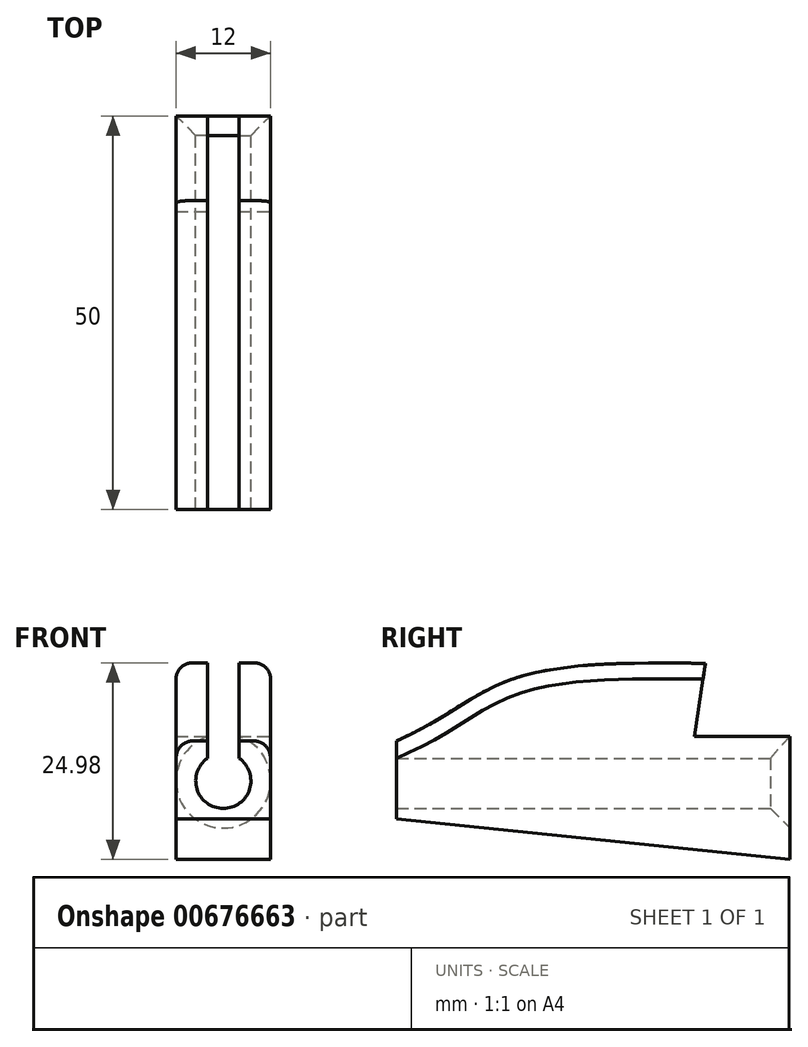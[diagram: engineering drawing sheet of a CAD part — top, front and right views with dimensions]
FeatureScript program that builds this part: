
annotation { "Feature Type Name" : "Feature", "Feature Type Description" : "" }
export const myFeature = defineFeature(function(context is Context, id is Id, definition is map)
    precondition{}
    {
        {
            var Q0;
            Q0=qCreatedBy(makeId("Top.planeOp"),FACE);
            var sketch = newSketch(context, id + "F0", { "sketchPlane" : qUnion([Q0])});
            skLineSegment(sketch, "E0.bottom", {"start": v(-6, 0) * mm, "end": v(6, 0) * mm});
            skLineSegment(sketch, "E0.top", {"start": v(-6, -50) * mm, "end": v(6, -50) * mm});
            skLineSegment(sketch, "E0.left", {"start": v(-6, 0) * mm, "end": v(-6, -50) * mm});
            skLineSegment(sketch, "E0.right", {"start": v(6, 0) * mm, "end": v(6, -50) * mm});
            skSolve(sketch);
        }
        {
            var Q0;
            Q0=makeQuery(id+"F0.imprint","IMPRINT",FACE,{"disambiguationData":[TD([[makeQuery(id+"F0.imprint","IMPRINT",EDGE,{"derivedFrom":sQuery(id+"F0.wireOp",EDGE,"E0.bottom")}),-1.0]])]});
            extrude(context, id + "F1", {"entities" : qUnion([Q0]), "depth" : 30 * mm, "offsetDistance" : 25 * mm});
        }
        {
            var Q0;
            Q0=qCreatedBy(makeId("Front.planeOp"),FACE);
            var sketch = newSketch(context, id + "F2", { "sketchPlane" : qUnion([Q0])});
            skCircle(sketch, "E1", {"center": v(0, 10) * mm, "radius": 3.5 * mm});
            skSolve(sketch);
        }
        {
            var Q0;
            Q0=sQuery(id+"F2.wireOp",VERTEX,"E1.center");
            var Q1;
            Q1=makeQuery(id+"F1.opExtrude","SWEPT_BODY",BODY,{"disambiguationData":[OSD([sQuery(id+"F0.wireOp",EDGE,"E0.bottom"),sQuery(id+"F0.wireOp",EDGE,"E0.top"),sQuery(id+"F0.wireOp",EDGE,"E0.left"),sQuery(id+"F0.wireOp",EDGE,"E0.right")])]});
            hole(context, id + "F3", {"style" : HoleStyle.C_SINK, "endStyle" : HoleEndStyle.THROUGH, "oppositeDirection" : true, "holeDiameter" : 7 * mm, "cSinkDiameter" : 12 * mm, "cSinkAngle" : 90 * degree, "majorDiameter" : 5 * mm, "isTappedThrough" : true, "tappedDepth" : 12 * mm, "tapClearance" : 3, "locations" : qUnion([Q0]), "scope" : qUnion([Q1])});
        }
        {
            var Q0;
            Q0=qCreatedBy(makeId("Front.planeOp"),FACE);
            var sketch = newSketch(context, id + "F4", { "sketchPlane" : qUnion([Q0])});
            skLineSegment(sketch, "E2.bottom", {"start": v(2, 30) * mm, "end": v(-2, 30) * mm});
            skLineSegment(sketch, "E2.top", {"start": v(2, 12.87) * mm, "end": v(-2, 12.87) * mm});
            skLineSegment(sketch, "E2.left", {"start": v(2, 30) * mm, "end": v(2, 12.87) * mm});
            skLineSegment(sketch, "E2.right", {"start": v(-2, 30) * mm, "end": v(-2, 12.87) * mm});
            skSolve(sketch);
        }
        {
            var Q0;
            Q0=makeQuery(id+"F4.imprint","IMPRINT",FACE,{"disambiguationData":[TD([[makeQuery(id+"F4.imprint","IMPRINT",EDGE,{"derivedFrom":sQuery(id+"F4.wireOp",EDGE,"E2.bottom")}),1.0]])]});
            extrude(context, id + "F5", {"entities" : qUnion([Q0]), "operationType" : NewBodyOperationType.REMOVE, "depth" : 50 * mm, "offsetDistance" : 25 * mm});
        }
        {
            var Q0;
            Q0=qCreatedBy(makeId("Right.planeOp"),FACE);
            var sketch = newSketch(context, id + "F6", { "sketchPlane" : qUnion([Q0])});
            skLineSegment(sketch, "E3", {"start": v(0, 15.66) * mm, "end": v(-12.16, 15.66) * mm});
            skLineSegment(sketch, "E4", {"start": v(-12.16, 15.66) * mm, "end": v(-10.75, 24.93) * mm});
            skSolve(sketch);
        }
        {
            var Q0;
            Q0=qCreatedBy(makeId("Right.planeOp"),FACE);
            var sketch = newSketch(context, id + "F7", { "sketchPlane" : qUnion([Q0])});
            skFitSpline(sketch, "E5", {"points": [v(-10.75, 24.93) * mm, v(-34.14, 22.02) * mm, v(-50, 15.06) * mm], "startDerivative": vector(-44.86, 0.18) * mm, "endDerivative": vector(-35.7, -18.77) * mm});
            skSolve(sketch);
        }
        {
            var Q0;
            Q0=qCreatedBy(makeId("Right.planeOp"),FACE);
            var sketch = newSketch(context, id + "F8", { "sketchPlane" : qUnion([Q0])});
            skLineSegment(sketch, "E6.0", {"start": v(0, 15.66) * mm, "end": v(-12.16, 15.66) * mm});
            skLineSegment(sketch, "E7.0", {"start": v(-12.16, 15.66) * mm, "end": v(-10.75, 24.93) * mm});
            skFitSpline(sketch, "E8.0", {"points": [v(-10.75, 24.93) * mm, v(-18.8, 24.96) * mm, v(-34.66, 23.13) * mm, v(-44.5, 17.95) * mm, v(-50, 15.06) * mm]});
            skLineSegment(sketch, "E9.0", {"start": v(-50, 30) * mm, "end": v(-50, 0) * mm});
            skLineSegment(sketch, "E10.0", {"start": v(0, 30) * mm, "end": v(-50, 30) * mm});
            skLineSegment(sketch, "E11.0.0", {"start": v(0, 0) * mm, "end": v(-50, 0) * mm});
            skLineSegment(sketch, "E11.0.1", {"start": v(-50, 0) * mm, "end": v(-50, 30) * mm});
            skLineSegment(sketch, "E11.0.2", {"start": v(-50, 30) * mm, "end": v(0, 30) * mm});
            skLineSegment(sketch, "E11.0.3", {"start": v(0, 30) * mm, "end": v(0, 10) * mm});
            skLineSegment(sketch, "E11.0.4", {"start": v(0, 10) * mm, "end": v(0, 0) * mm});
            skSolve(sketch);
        }
        {
            var Q0;
            Q0=qCreatedBy(makeId("Right.planeOp"),FACE);
            var sketch = newSketch(context, id + "F9", { "sketchPlane" : qUnion([Q0])});
            skLineSegment(sketch, "E12", {"start": v(0, 15.66) * mm, "end": v(0, 30) * mm});
            skLineSegment(sketch, "E13", {"start": v(0, 30) * mm, "end": v(-50, 30) * mm});
            skLineSegment(sketch, "E14", {"start": v(-50, 30) * mm, "end": v(-50, 15.06) * mm});
            skSolve(sketch);
        }
        {
            var Q0;
            Q0=qCreatedBy(makeId("Right.planeOp"),FACE);
            var sketch = newSketch(context, id + "F10", { "sketchPlane" : qUnion([Q0])});
            skLineSegment(sketch, "E15.0", {"start": v(0, 15.66) * mm, "end": v(0, 30) * mm});
            skLineSegment(sketch, "E15.1", {"start": v(0, 30) * mm, "end": v(-50, 30) * mm});
            skLineSegment(sketch, "E15.2", {"start": v(-50, 30) * mm, "end": v(-50, 15.06) * mm});
            skFitSpline(sketch, "E16.0", {"points": [v(-10.75, 24.93) * mm, v(-18.8, 24.96) * mm, v(-34.66, 23.13) * mm, v(-44.5, 17.95) * mm, v(-50, 15.06) * mm]});
            skLineSegment(sketch, "E17.0", {"start": v(-12.16, 15.66) * mm, "end": v(-10.75, 24.93) * mm});
            skLineSegment(sketch, "E18.0", {"start": v(0, 15.66) * mm, "end": v(-12.16, 15.66) * mm});
            skSolve(sketch);
        }
        {
            var Q0;
            Q0 = qSketchRegion(id + "F10", true);
            extrude(context, id + "F11", {"entities" : qUnion([Q0]), "operationType" : NewBodyOperationType.REMOVE, "endBound" : BoundingType.SYMMETRIC, "oppositeDirection" : true, "depth" : 25 * mm, "offsetDistance" : 25 * mm});
        }
        {
            var Q0;
            Q0=makeQuery(id+"F11.boolean.opBoolean","INTERSECT",EDGE,{"derivedFrom":[makeQuery(id+"F1.opExtrude","SWEPT_FACE",FACE,{"disambiguationData":[OSD([sQuery(id+"F0.wireOp",EDGE,"E0.left")])]}),makeQuery(id+"F11.opExtrude","SWEPT_FACE",FACE,{"disambiguationData":[OSD([sQuery(id+"F10.wireOp",EDGE,"E16.0")])]})]});
            fillet(context, id + "F12", {"entities" : qUnion([Q0]), "radius" : 2 * mm, "tangentPropagation" : true, "allowEdgeOverflow" : false});
        }
        {
            var Q0;
            Q0=makeQuery(id+"F11.boolean.opBoolean","INTERSECT",EDGE,{"derivedFrom":[makeQuery(id+"F1.opExtrude","SWEPT_FACE",FACE,{"disambiguationData":[OSD([sQuery(id+"F0.wireOp",EDGE,"E0.right")])]}),makeQuery(id+"F11.opExtrude","SWEPT_FACE",FACE,{"disambiguationData":[OSD([sQuery(id+"F10.wireOp",EDGE,"E16.0")])]})]});
            fillet(context, id + "F13", {"entities" : qUnion([Q0]), "radius" : 2 * mm, "tangentPropagation" : true, "allowEdgeOverflow" : false});
        }
        {
            var Q0;
            Q0=qCreatedBy(makeId("Right.planeOp"),FACE);
            var sketch = newSketch(context, id + "F14", { "sketchPlane" : qUnion([Q0])});
            skLineSegment(sketch, "E19", {"start": v(-50, 5.2) * mm, "end": v(0, 0) * mm});
            skLineSegment(sketch, "E20", {"start": v(0, 0) * mm, "end": v(0, 0) * mm});
            skLineSegment(sketch, "E21", {"start": v(0, 0) * mm, "end": v(-50, 0) * mm});
            skLineSegment(sketch, "E22", {"start": v(-50, 0) * mm, "end": v(-50, 5.2) * mm});
            skSolve(sketch);
        }
        {
            var Q0;
            Q0 = qSketchRegion(id + "F14", true);
            extrude(context, id + "F15", {"entities" : qUnion([Q0]), "operationType" : NewBodyOperationType.REMOVE, "endBound" : BoundingType.SYMMETRIC, "oppositeDirection" : true, "depth" : 25 * mm, "offsetDistance" : 25 * mm});
        }
    });
